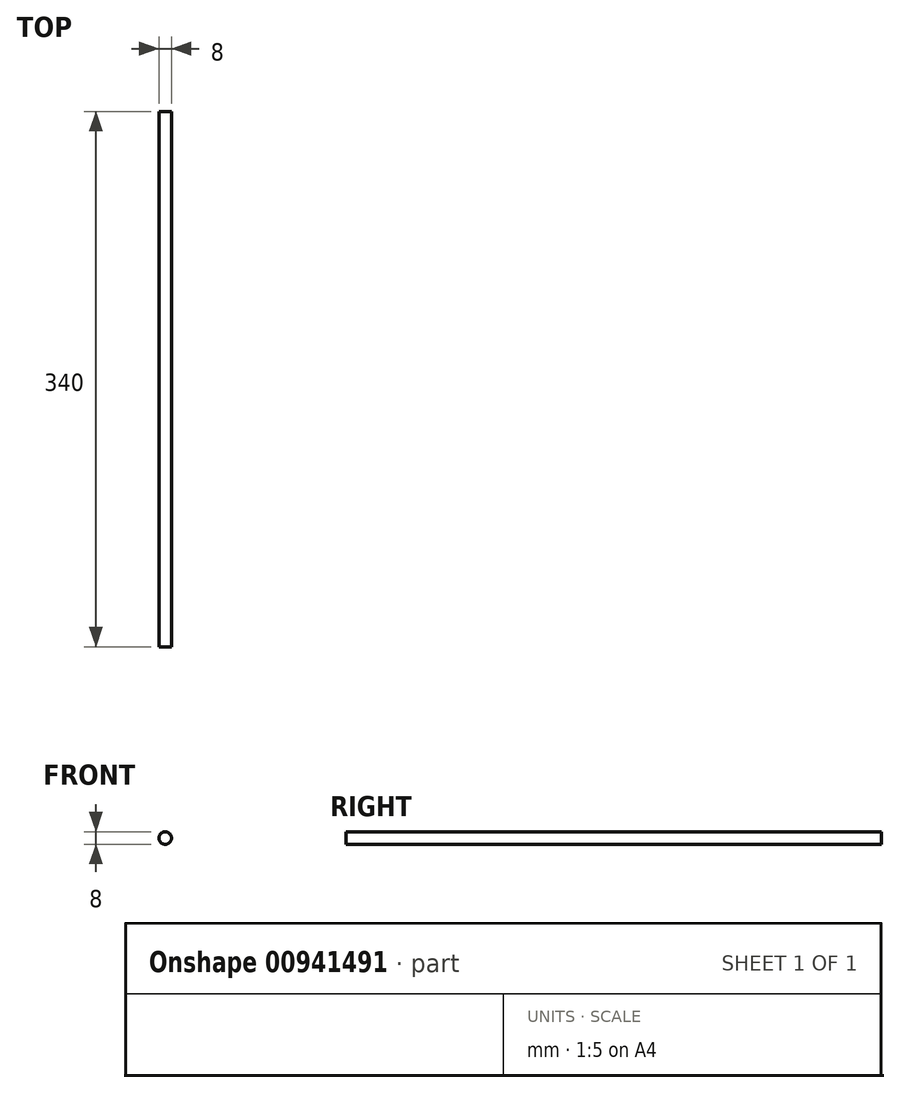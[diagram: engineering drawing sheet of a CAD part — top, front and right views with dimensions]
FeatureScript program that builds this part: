
annotation { "Feature Type Name" : "Feature", "Feature Type Description" : "" }
export const myFeature = defineFeature(function(context is Context, id is Id, definition is map)
    precondition{}
    {
        {
            var Q0;
            Q0=qCreatedBy(makeId("Front.planeOp"),FACE);
            var sketch = newSketch(context, id + "F0", { "sketchPlane" : qUnion([Q0])});
            skCircle(sketch, "E0", {"center": v(0, 0) * mm, "radius": 4 * mm});
            skSolve(sketch);
        }
        {
            var Q0;
            Q0=makeQuery(id+"F0.imprint","IMPRINT",FACE,{"disambiguationData":[TD([[makeQuery(id+"F0.imprint","IMPRINT",EDGE,{"derivedFrom":sQuery(id+"F0.wireOp",EDGE,"E0")}),1.0]])]});
            extrude(context, id + "F1", {"entities" : qUnion([Q0]), "depth" : 340 * mm, "offsetDistance" : 25 * mm});
        }
    });
